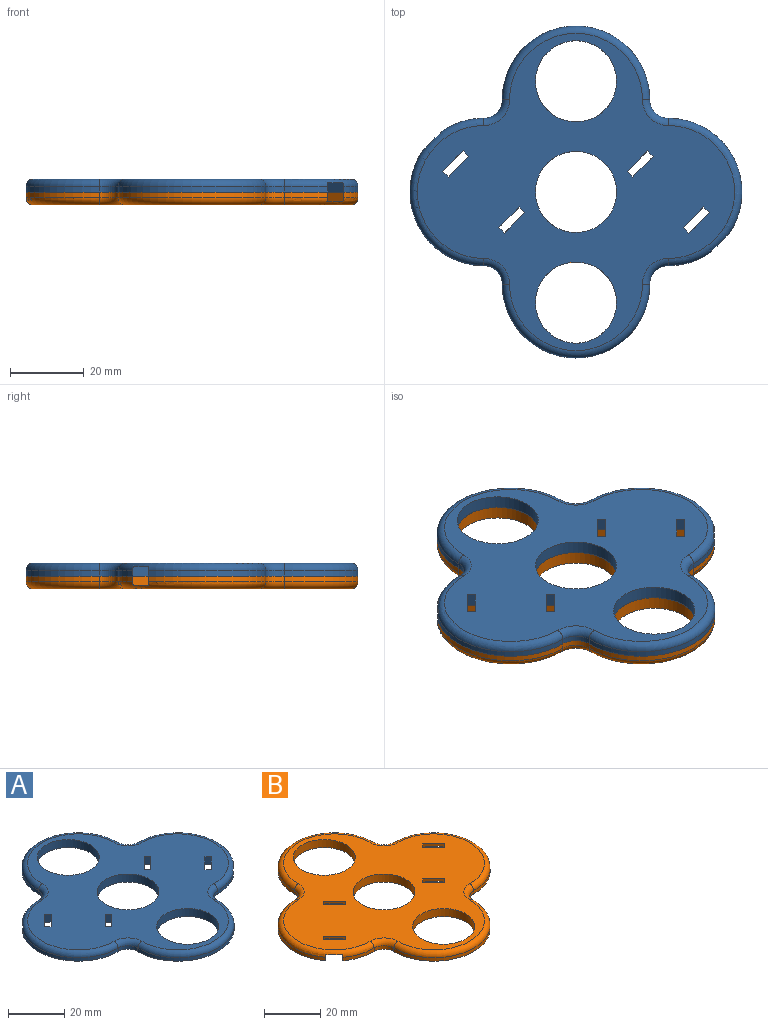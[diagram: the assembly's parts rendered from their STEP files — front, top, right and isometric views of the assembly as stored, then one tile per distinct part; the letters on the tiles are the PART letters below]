
ASSEMBLY  parts=2 mates=1
PART A: 79 faces, bbox 93.3x93.3x4.5 mm
  f0: cylinder r=20mm len=31.86mm, axis (0,0,-1), area 66.2mm2, adj f2,f15,f22,f67
  f1: cylinder r=20mm len=31.86mm, axis (0,0,-1), area 66.2mm2, adj f2,f26,f37,f74
  f2: plane 90x90mm, normal (0,0,-1), area 2805.7mm2, adj f0,f1,f6,f7,f8,f9,f12,f13
  f3: plane 86x86mm, normal (0,0,1), area 3172.3mm2, adj f27,f29,f30,f43,f44,f45,f46,f47
  f4: plane 17.9x17.9mm, normal (0,0,-1), area 115.9mm2, adj f6,f8,f52,f55
  f5: plane 11.34x11.34mm, normal (0,0,-1), area 60.2mm2, adj f7,f9,f38,f51
  f6: plane 13.66x13.66mm, normal (-0.71,-0.71,0), area 16.8mm2, adj f2,f4,f18,f19,f52,f55
  f7: plane 7.1x7.1mm, normal (-0.71,-0.71,0), area 25.1mm2, adj f2,f5,f38,f51
  f8: plane 13.66x13.66mm, normal (0.71,0.71,0), area 16.8mm2, adj f2,f4,f33,f34,f52,f55
  f9: plane 7.1x7.1mm, normal (0.71,0.71,0), area 25.1mm2, adj f2,f5,f38,f51
  f10: plane 17.9x17.9mm, normal (0,0,-1), area 115.9mm2, adj f12,f14,f43,f48
  f11: plane 9.65x9.65mm, normal (0,0,-1), area 46.8mm2, adj f13,f15,f44,f67
  f12: plane 13.66x13.66mm, normal (0.71,0.71,0), area 16.8mm2, adj f2,f10,f16,f17,f43,f48
  f13: plane 5.62x5.62mm, normal (0.71,0.71,0), area 19.7mm2, adj f2,f11,f23,f44,f67
  f14: plane 13.66x13.66mm, normal (-0.71,-0.71,0), area 16.8mm2, adj f2,f10,f31,f32,f43,f48
  f15: plane 5.62x5.62mm, normal (-0.71,-0.71,0), area 19.7mm2, adj f0,f2,f11,f44,f67
  f16: cylinder r=10mm len=14.62mm, axis (0,0,-1), area 41.8mm2, adj f2,f12,f17
  f17: plane 14.62x14.62mm, normal (0,0,-1), area 98mm2, adj f12,f16
  f18: cylinder r=10mm len=14.62mm, axis (0,0,-1), area 41.8mm2, adj f2,f6,f19
  f19: plane 14.62x14.62mm, normal (0,0,-1), area 98mm2, adj f6,f18
  f20: cylinder r=5mm len=5mm, axis (0,0,-1), area 11.8mm2, adj f2,f21,f28,f73
  f21: cylinder r=20mm len=40mm, axis (0,0,-1), area 94.2mm2, adj f2,f20,f22,f71
  f22: cylinder r=5mm len=5mm, axis (0,0,-1), area 11.8mm2, adj f0,f2,f21,f69
  f23: cylinder r=20mm len=11.86mm, axis (0,0,-1), area 19mm2, adj f2,f13,f24,f67
  f24: cylinder r=5mm len=5mm, axis (0,0,-1), area 11.8mm2, adj f2,f23,f25,f68
  f25: cylinder r=20mm len=40mm, axis (0,0,-1), area 94.2mm2, adj f2,f24,f26,f70
  f26: cylinder r=5mm len=5mm, axis (0,0,-1), area 11.8mm2, adj f1,f2,f25,f72
  f27: cylinder r=11mm len=22mm, axis (0,0,-1), area 241.9mm2, adj f2,f3
  f28: cylinder r=20mm len=11.86mm, axis (0,0,-1), area 19mm2, adj f2,f20,f36,f74
  f29: cylinder r=11mm len=22mm, axis (0,0,-1), area 241.9mm2, adj f2,f3
  f30: cylinder r=11mm len=22mm, axis (0,0,-1), area 241.9mm2, adj f2,f3
  f31: cylinder r=10mm len=14.62mm, axis (0,0,-1), area 41.8mm2, adj f2,f14,f32
  f32: plane 14.62x14.62mm, normal (0,0,-1), area 98mm2, adj f14,f31
  f33: cylinder r=10mm len=14.62mm, axis (0,0,-1), area 41.8mm2, adj f2,f8,f34
  f34: plane 14.62x14.62mm, normal (0,0,-1), area 98mm2, adj f8,f33
  f35: plane 9.65x9.65mm, normal (0,0,-1), area 46.8mm2, adj f36,f37,f56,f74
  f36: plane 5.62x5.62mm, normal (-0.71,-0.71,0), area 19.7mm2, adj f2,f28,f35,f56,f74
  f37: plane 5.62x5.62mm, normal (0.71,0.71,0), area 19.7mm2, adj f1,f2,f35,f56,f74
  f38: plane 4.24x4.24mm, normal (-0.71,0.71,0), area 15mm2, adj f2,f5,f7,f9
  f39: plane 11.34x11.34mm, normal (0,0,-1), area 60.2mm2, adj f40,f41,f42,f47
  f40: plane 7.1x7.1mm, normal (0.71,0.71,0), area 25.1mm2, adj f2,f39,f42,f47
  f41: plane 7.1x7.1mm, normal (-0.71,-0.71,0), area 25.1mm2, adj f2,f39,f42,f47
  f42: plane 4.24x4.24mm, normal (0.71,-0.71,0), area 15mm2, adj f2,f39,f40,f41
  f43: plane 5.56x5.56mm, normal (0.71,-0.71,0), area 12.5mm2, adj f2,f3,f10,f12,f14,f45,f46
  f44: plane 5.56x5.56mm, normal (-0.71,0.71,0), area 12.5mm2, adj f2,f3,f11,f13,f15,f45,f46
  f45: plane 3.5x1.56mm, normal (-0.71,-0.71,0), area 7.7mm2, adj f2,f3,f43,f44
  f46: plane 3.5x1.56mm, normal (0.71,0.71,0), area 7.7mm2, adj f2,f3,f43,f44
  f47: plane 5.56x5.56mm, normal (0.71,-0.71,0), area 12.5mm2, adj f2,f3,f39,f40,f41,f49,f50
  f48: plane 5.56x5.56mm, normal (-0.71,0.71,0), area 12.5mm2, adj f2,f3,f10,f12,f14,f49,f50
  f49: plane 3.5x1.56mm, normal (-0.71,-0.71,0), area 7.7mm2, adj f2,f3,f47,f48
  f50: plane 3.5x1.56mm, normal (0.71,0.71,0), area 7.7mm2, adj f2,f3,f47,f48
  f51: plane 5.56x5.56mm, normal (-0.71,0.71,0), area 12.5mm2, adj f2,f3,f5,f7,f9,f53,f54
  f52: plane 5.56x5.56mm, normal (0.71,-0.71,0), area 12.5mm2, adj f2,f3,f4,f6,f8,f53,f54
  f53: plane 3.5x1.56mm, normal (-0.71,-0.71,0), area 7.7mm2, adj f2,f3,f51,f52
  f54: plane 3.5x1.56mm, normal (0.71,0.71,0), area 7.7mm2, adj f2,f3,f51,f52
  f55: plane 5.56x5.56mm, normal (-0.71,0.71,0), area 12.5mm2, adj f2,f3,f4,f6,f8,f57,f58
  f56: plane 5.56x5.56mm, normal (0.71,-0.71,0), area 12.5mm2, adj f2,f3,f35,f36,f37,f57,f58
  f57: plane 3.5x1.56mm, normal (-0.71,-0.71,0), area 7.7mm2, adj f2,f3,f55,f56
  f58: plane 3.5x1.56mm, normal (0.71,0.71,0), area 7.7mm2, adj f2,f3,f55,f56
  f59: cylinder r=2.5mm len=5mm, axis (0,0,1), area 7.9mm2, adj f2,f78
  f60: plane 4x4mm, normal (0,0,-1), area 12.6mm2, adj f78
  f61: cylinder r=2.5mm len=5mm, axis (0,0,1), area 7.9mm2, adj f2,f77
  f62: plane 4x4mm, normal (0,0,-1), area 12.6mm2, adj f77
  f63: cylinder r=2.5mm len=5mm, axis (0,0,1), area 7.9mm2, adj f2,f76
  f64: plane 4x4mm, normal (0,0,-1), area 12.6mm2, adj f76
  f65: cylinder r=2.5mm len=5mm, axis (0,0,1), area 7.9mm2, adj f2,f75
  f66: plane 4x4mm, normal (0,0,-1), area 12.6mm2, adj f75
  f67: torus R=18mm, axis (0,0,1), area 183.9mm2, adj f0,f3,f11,f13,f15,f23,f68,f69
  f68: torus R=7mm, axis (0,0,1), area 28.3mm2, adj f3,f24,f67,f70
  f69: torus R=7mm, axis (0,0,1), area 28.3mm2, adj f3,f22,f67,f71
  f70: torus R=18mm, axis (0,0,1), area 190.2mm2, adj f3,f25,f68,f72
  f71: torus R=18mm, axis (0,0,1), area 190.2mm2, adj f3,f21,f69,f73
  f72: torus R=7mm, axis (0,0,1), area 28.3mm2, adj f3,f26,f70,f74
  f73: torus R=7mm, axis (0,0,1), area 28.3mm2, adj f3,f20,f71,f74
  f74: torus R=18mm, axis (0,0,1), area 183.9mm2, adj f1,f3,f28,f35,f36,f37,f72,f73
  f75: torus R=2mm, axis (0,0,-1), area 11.4mm2, adj f65,f66
  f76: torus R=2mm, axis (0,0,-1), area 11.4mm2, adj f63,f64
  f77: torus R=2mm, axis (0,0,-1), area 11.4mm2, adj f61,f62
  f78: torus R=2mm, axis (0,0,-1), area 11.4mm2, adj f59,f60
PART B: 75 faces, bbox 93.3x93.3x3.5 mm
  f0: cylinder r=20mm len=11.86mm, axis (0,0,-1), area 19mm2, adj f2,f20,f36,f70
  f1: cylinder r=20mm len=11.86mm, axis (0,0,-1), area 19mm2, adj f2,f13,f24,f71
  f2: plane 90x90mm, normal (0,0,-1), area 2805.7mm2, adj f0,f1,f6,f7,f8,f9,f12,f13
  f3: plane 86x86mm, normal (0,0,1), area 3172.3mm2, adj f27,f29,f30,f43,f44,f45,f46,f47
  f4: plane 17.9x17.9mm, normal (0,0,-1), area 115.9mm2, adj f6,f8,f52,f55
  f5: plane 11.34x11.34mm, normal (0,0,-1), area 60.2mm2, adj f7,f9,f38,f51
  f6: plane 13.66x13.66mm, normal (-0.71,0.71,0), area 16.8mm2, adj f2,f4,f18,f19,f52,f55
  f7: plane 7.1x7.1mm, normal (-0.71,0.71,0), area 25.1mm2, adj f2,f5,f38,f51
  f8: plane 13.66x13.66mm, normal (0.71,-0.71,0), area 16.8mm2, adj f2,f4,f33,f34,f52,f55
  f9: plane 7.1x7.1mm, normal (0.71,-0.71,0), area 25.1mm2, adj f2,f5,f38,f51
  f10: plane 17.9x17.9mm, normal (0,0,-1), area 115.9mm2, adj f12,f14,f43,f48
  f11: plane 9.65x9.65mm, normal (0,0,-1), area 46.8mm2, adj f13,f15,f44,f71
  f12: plane 13.66x13.66mm, normal (0.71,-0.71,0), area 16.8mm2, adj f2,f10,f16,f17,f43,f48
  f13: plane 5.62x5.62mm, normal (0.71,-0.71,0), area 19.7mm2, adj f1,f2,f11,f44,f71
  f14: plane 13.66x13.66mm, normal (-0.71,0.71,0), area 16.8mm2, adj f2,f10,f31,f32,f43,f48
  f15: plane 5.62x5.62mm, normal (-0.71,0.71,0), area 19.7mm2, adj f2,f11,f23,f44,f71
  f16: cylinder r=10mm len=14.62mm, axis (0,0,-1), area 41.8mm2, adj f2,f12,f17
  f17: plane 14.62x14.62mm, normal (0,0,-1), area 98mm2, adj f12,f16
  f18: cylinder r=10mm len=14.62mm, axis (0,0,-1), area 41.8mm2, adj f2,f6,f19
  f19: plane 14.62x14.62mm, normal (0,0,-1), area 98mm2, adj f6,f18
  f20: cylinder r=5mm len=5mm, axis (0,0,-1), area 11.8mm2, adj f0,f2,f21,f72
  f21: cylinder r=20mm len=40mm, axis (0,0,-1), area 94.2mm2, adj f2,f20,f22,f74
  f22: cylinder r=5mm len=5mm, axis (0,0,-1), area 11.8mm2, adj f2,f21,f23,f73
  f23: cylinder r=20mm len=31.86mm, axis (0,0,-1), area 66.2mm2, adj f2,f15,f22,f71
  f24: cylinder r=5mm len=5mm, axis (0,0,-1), area 11.8mm2, adj f1,f2,f25,f69
  f25: cylinder r=20mm len=40mm, axis (0,0,-1), area 94.2mm2, adj f2,f24,f26,f67
  f26: cylinder r=5mm len=5mm, axis (0,0,-1), area 11.8mm2, adj f2,f25,f28,f68
  f27: cylinder r=11mm len=22mm, axis (0,0,-1), area 241.9mm2, adj f2,f3
  f28: cylinder r=20mm len=31.86mm, axis (0,0,-1), area 66.2mm2, adj f2,f26,f37,f70
  f29: cylinder r=11mm len=22mm, axis (0,0,-1), area 241.9mm2, adj f2,f3
  f30: cylinder r=11mm len=22mm, axis (0,0,-1), area 241.9mm2, adj f2,f3
  f31: cylinder r=10mm len=14.62mm, axis (0,0,-1), area 41.8mm2, adj f2,f14,f32
  f32: plane 14.62x14.62mm, normal (0,0,-1), area 98mm2, adj f14,f31
  f33: cylinder r=10mm len=14.62mm, axis (0,0,-1), area 41.8mm2, adj f2,f8,f34
  f34: plane 14.62x14.62mm, normal (0,0,-1), area 98mm2, adj f8,f33
  f35: plane 9.65x9.65mm, normal (0,0,-1), area 46.8mm2, adj f36,f37,f56,f70
  f36: plane 5.62x5.62mm, normal (-0.71,0.71,0), area 19.7mm2, adj f0,f2,f35,f56,f70
  f37: plane 5.62x5.62mm, normal (0.71,-0.71,0), area 19.7mm2, adj f2,f28,f35,f56,f70
  f38: plane 4.24x4.24mm, normal (-0.71,-0.71,0), area 15mm2, adj f2,f5,f7,f9
  f39: plane 11.34x11.34mm, normal (0,0,-1), area 60.2mm2, adj f40,f41,f42,f47
  f40: plane 7.1x7.1mm, normal (0.71,-0.71,0), area 25.1mm2, adj f2,f39,f42,f47
  f41: plane 7.1x7.1mm, normal (-0.71,0.71,0), area 25.1mm2, adj f2,f39,f42,f47
  f42: plane 4.24x4.24mm, normal (0.71,0.71,0), area 15mm2, adj f2,f39,f40,f41
  f43: plane 5.56x5.56mm, normal (0.71,0.71,0), area 12.5mm2, adj f2,f3,f10,f12,f14,f45,f46
  f44: plane 5.56x5.56mm, normal (-0.71,-0.71,0), area 12.5mm2, adj f2,f3,f11,f13,f15,f45,f46
  f45: plane 3.5x1.56mm, normal (-0.71,0.71,0), area 7.7mm2, adj f2,f3,f43,f44
  f46: plane 3.5x1.56mm, normal (0.71,-0.71,0), area 7.7mm2, adj f2,f3,f43,f44
  f47: plane 5.56x5.56mm, normal (0.71,0.71,0), area 12.5mm2, adj f2,f3,f39,f40,f41,f49,f50
  f48: plane 5.56x5.56mm, normal (-0.71,-0.71,0), area 12.5mm2, adj f2,f3,f10,f12,f14,f49,f50
  f49: plane 3.5x1.56mm, normal (-0.71,0.71,0), area 7.7mm2, adj f2,f3,f47,f48
  f50: plane 3.5x1.56mm, normal (0.71,-0.71,0), area 7.7mm2, adj f2,f3,f47,f48
  f51: plane 5.56x5.56mm, normal (-0.71,-0.71,0), area 12.5mm2, adj f2,f3,f5,f7,f9,f53,f54
  f52: plane 5.56x5.56mm, normal (0.71,0.71,0), area 12.5mm2, adj f2,f3,f4,f6,f8,f53,f54
  f53: plane 3.5x1.56mm, normal (-0.71,0.71,0), area 7.7mm2, adj f2,f3,f51,f52
  f54: plane 3.5x1.56mm, normal (0.71,-0.71,0), area 7.7mm2, adj f2,f3,f51,f52
  f55: plane 5.56x5.56mm, normal (-0.71,-0.71,0), area 12.5mm2, adj f2,f3,f4,f6,f8,f57,f58
  f56: plane 5.56x5.56mm, normal (0.71,0.71,0), area 12.5mm2, adj f2,f3,f35,f36,f37,f57,f58
  f57: plane 3.5x1.56mm, normal (-0.71,0.71,0), area 7.7mm2, adj f2,f3,f55,f56
  f58: plane 3.5x1.56mm, normal (0.71,-0.71,0), area 7.7mm2, adj f2,f3,f55,f56
  f59: cylinder r=2.5mm len=5mm, axis (0,0,-1), area 23.6mm2, adj f2,f60
  f60: plane 5x5mm, normal (0,0,-1), area 19.6mm2, adj f59
  f61: cylinder r=2.5mm len=5mm, axis (0,0,-1), area 23.6mm2, adj f2,f62
  f62: plane 5x5mm, normal (0,0,-1), area 19.6mm2, adj f61
  f63: cylinder r=2.5mm len=5mm, axis (0,0,-1), area 23.6mm2, adj f2,f64
  f64: plane 5x5mm, normal (0,0,-1), area 19.6mm2, adj f63
  f65: cylinder r=2.5mm len=5mm, axis (0,0,-1), area 23.6mm2, adj f2,f66
  f66: plane 5x5mm, normal (0,0,-1), area 19.6mm2, adj f65
  f67: torus R=18mm, axis (0,0,1), area 190.2mm2, adj f3,f25,f68,f69
  f68: torus R=7mm, axis (0,0,1), area 28.3mm2, adj f3,f26,f67,f70
  f69: torus R=7mm, axis (0,0,1), area 28.3mm2, adj f3,f24,f67,f71
  f70: torus R=18mm, axis (0,0,1), area 183.9mm2, adj f0,f3,f28,f35,f36,f37,f68,f72
  f71: torus R=18mm, axis (0,0,1), area 183.9mm2, adj f1,f3,f11,f13,f15,f23,f69,f73
  f72: torus R=7mm, axis (0,0,1), area 28.3mm2, adj f3,f20,f70,f74
  f73: torus R=7mm, axis (0,0,1), area 28.3mm2, adj f3,f22,f71,f74
  f74: torus R=18mm, axis (0,0,1), area 190.2mm2, adj f3,f21,f72,f73
PLACE A t=(29.38,-85.62,-8.99)mm
PLACE B rot(axis=(0,1,0),180deg) t=(29.38,20.38,-8.99)mm
MATE fastened B.f27 <-> A.f27  axis (0,0,1) through (29.38,20.38,-8.99)mm
